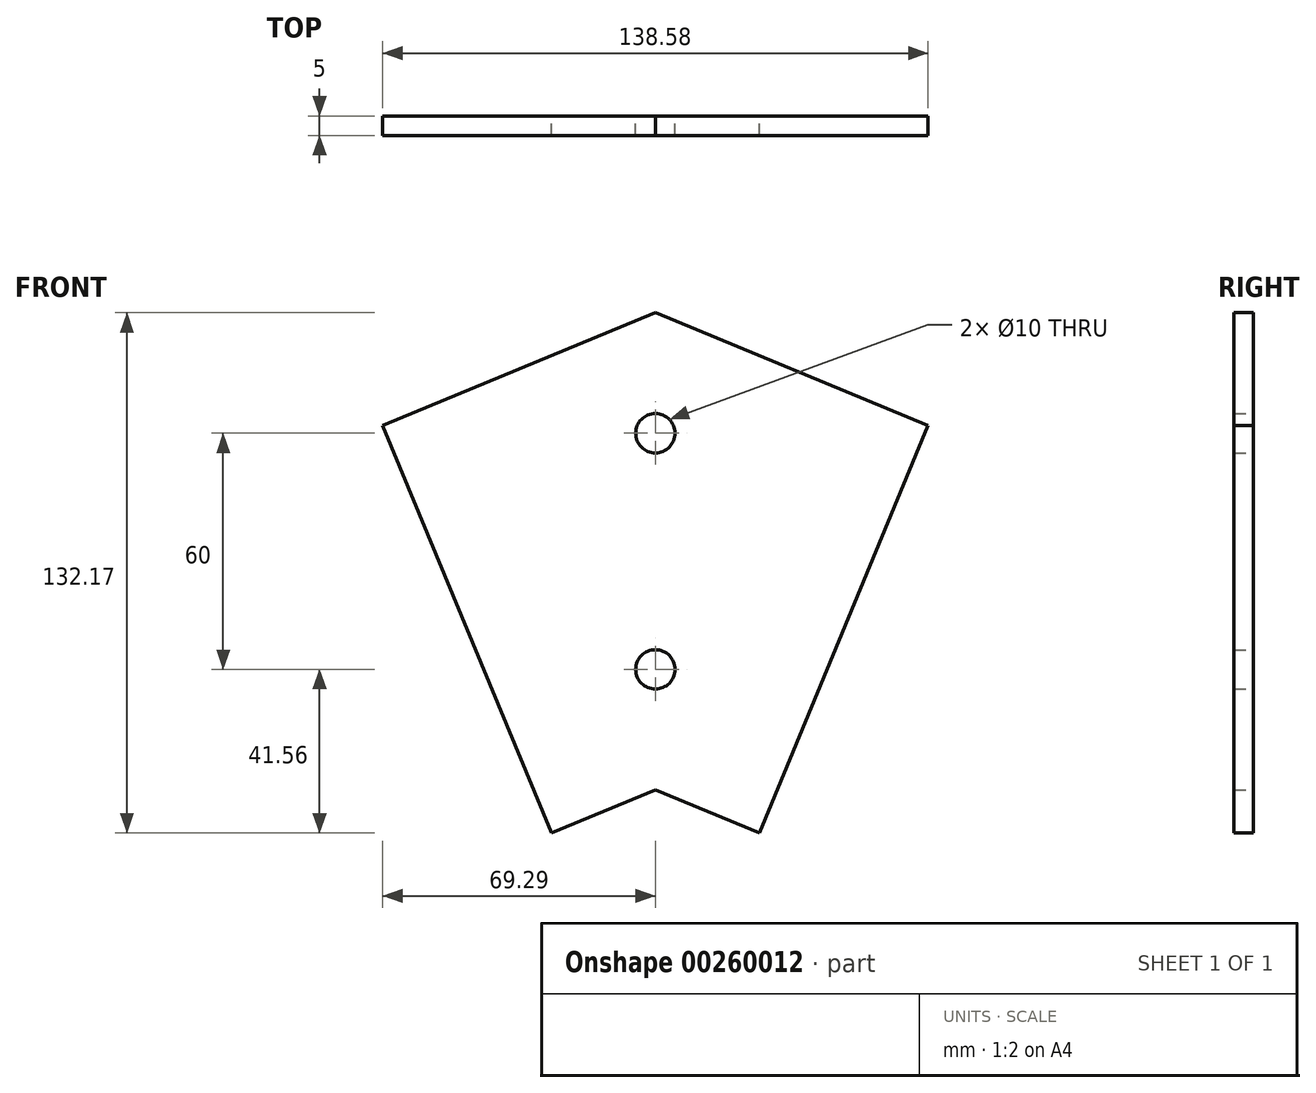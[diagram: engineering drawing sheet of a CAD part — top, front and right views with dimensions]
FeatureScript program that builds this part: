
annotation { "Feature Type Name" : "Feature", "Feature Type Description" : "" }
export const myFeature = defineFeature(function(context is Context, id is Id, definition is map)
    precondition{}
    {
        {
            var Q0;
            Q0=qCreatedBy(makeId("Front.planeOp"),FACE);
            var sketch = newSketch(context, id + "F0", { "sketchPlane" : qUnion([Q0])});
            skLineSegment(sketch, "E0", {"start": v(0, 192.98) * mm, "end": v(0, -198.78) * mm, "construction": true});
            skLineSegment(sketch, "E1", {"start": v(0, 157.88) * mm, "end": v(69.3, 129.18) * mm});
            skLineSegment(sketch, "E2", {"start": v(69.3, 129.18) * mm, "end": v(47.86, 77.45) * mm});
            skLineSegment(sketch, "E3", {"start": v(47.86, 77.45) * mm, "end": v(26.43, 25.7) * mm});
            skLineSegment(sketch, "E4", {"start": v(26.43, 25.7) * mm, "end": v(0, 36.66) * mm});
            skLineSegment(sketch, "E5", {"start": v(47.86, 77.45) * mm, "end": v(0, 97.27) * mm, "construction": true});
            skLineSegment(sketch, "E6.MirrorCS", {"start": v(-47.86, 77.45) * mm, "end": v(0, 97.27) * mm, "construction": true});
            skLineSegment(sketch, "E7.MirrorCS", {"start": v(-26.43, 25.7) * mm, "end": v(0, 36.66) * mm});
            skLineSegment(sketch, "E8.MirrorCS", {"start": v(-69.3, 129.18) * mm, "end": v(-47.86, 77.45) * mm});
            skLineSegment(sketch, "E9.MirrorCS", {"start": v(-47.86, 77.45) * mm, "end": v(-26.43, 25.7) * mm});
            skLineSegment(sketch, "E10.MirrorCS", {"start": v(0, 157.88) * mm, "end": v(-69.3, 129.18) * mm});
            skCircle(sketch, "E11", {"center": v(0, 127.27) * mm, "radius": 5 * mm});
            skCircle(sketch, "E12", {"center": v(0, 67.27) * mm, "radius": 5 * mm});
            skPoint(sketch, "E13", {"position": v(-23.93, 87.36) * mm});
            skLineSegment(sketch, "E14", {"start": v(0, 157.88) * mm, "end": v(-73.83, 188.46) * mm, "construction": true});
            skSolve(sketch);
        }
        {
            var Q0;
            Q0 = qSketchRegion(id + "F0", true);
            extrude(context, id + "F1", {"entities" : qUnion([Q0]), "depth" : 5 * mm});
        }
    });
